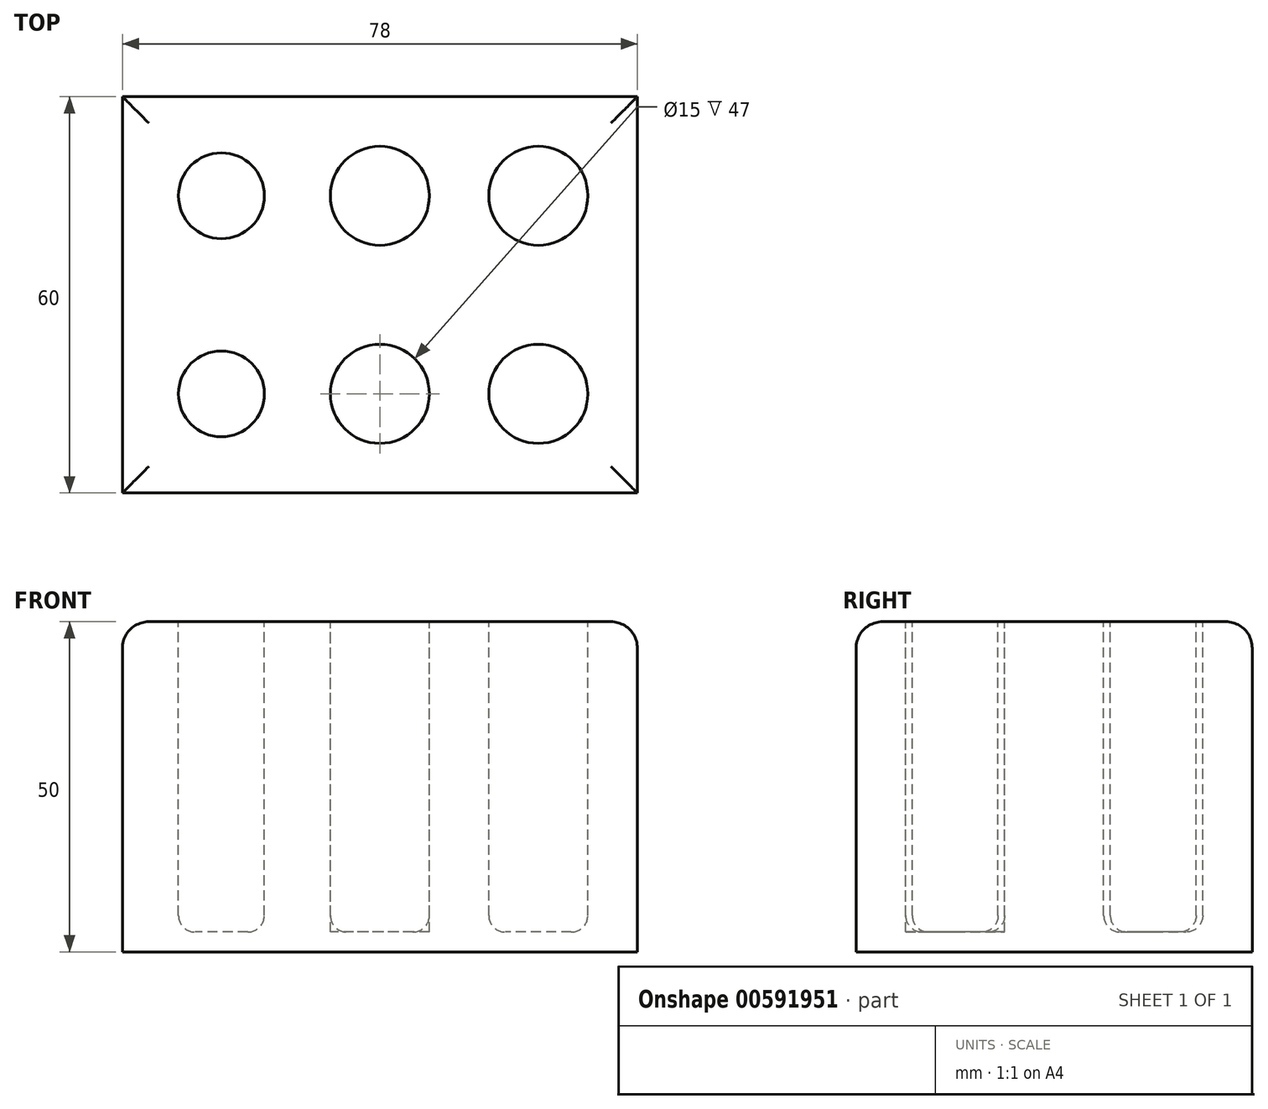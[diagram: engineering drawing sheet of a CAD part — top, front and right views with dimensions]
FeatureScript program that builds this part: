
annotation { "Feature Type Name" : "Feature", "Feature Type Description" : "" }
export const myFeature = defineFeature(function(context is Context, id is Id, definition is map)
    precondition{}
    {
        {
            var Q0;
            Q0=qCreatedBy(makeId("Top.planeOp"),FACE);
            var sketch = newSketch(context, id + "F0", { "sketchPlane" : qUnion([Q0])});
            skLineSegment(sketch, "E0.bottom", {"start": v(39, 30) * mm, "end": v(-39, 30) * mm});
            skLineSegment(sketch, "E0.top", {"start": v(39, -30) * mm, "end": v(-39, -30) * mm});
            skLineSegment(sketch, "E0.left", {"start": v(39, 30) * mm, "end": v(39, -30) * mm});
            skLineSegment(sketch, "E0.right", {"start": v(-39, 30) * mm, "end": v(-39, -30) * mm});
            skPoint(sketch, "E0.middle", {"position": v(0, 0) * mm});
            skCircle(sketch, "E1", {"center": v(-24, 15) * mm, "radius": 7.5 * mm});
            skCircle(sketch, "E2.0.1.0", {"center": v(-24, -15) * mm, "radius": 7.5 * mm});
            skCircle(sketch, "E2.1.0.0", {"center": v(0, 15) * mm, "radius": 7.5 * mm});
            skCircle(sketch, "E2.1.1.0", {"center": v(0, -15) * mm, "radius": 7.5 * mm});
            skCircle(sketch, "E2.2.0.0", {"center": v(24, 15) * mm, "radius": 7.5 * mm});
            skCircle(sketch, "E2.2.1.0", {"center": v(24, -15) * mm, "radius": 7.5 * mm});
            skLineSegment(sketch, "E2.direction1", {"start": v(-24, 15) * mm, "end": v(0, 15) * mm, "construction": true});
            skLineSegment(sketch, "E2.direction2", {"start": v(-24, 15) * mm, "end": v(-24, -15) * mm, "construction": true});
            skCircle(sketch, "E3", {"center": v(-24, 15) * mm, "radius": 6.5 * mm});
            skCircle(sketch, "E4", {"center": v(-24, -15) * mm, "radius": 6.5 * mm});
            skLineSegment(sketch, "E5", {"start": v(24, 30) * mm, "end": v(24, 15) * mm, "construction": true});
            skLineSegment(sketch, "E6", {"start": v(24, -15) * mm, "end": v(24, -30) * mm, "construction": true});
            skLineSegment(sketch, "E7", {"start": v(-24, -15) * mm, "end": v(-39, -15) * mm, "construction": true});
            skLineSegment(sketch, "E8", {"start": v(24, -15) * mm, "end": v(39, -15) * mm, "construction": true});
            skSolve(sketch);
        }
        {
            var Q0;
            Q0=makeQuery(id+"F0.imprint","IMPRINT",FACE,{"disambiguationData":[TD([[makeQuery(id+"F0.imprint","IMPRINT",EDGE,{"derivedFrom":sQuery(id+"F0.wireOp",EDGE,"E0.bottom")}),1.0]])]});
            var Q1;
            Q1=makeQuery(id+"F0.imprint","IMPRINT",FACE,{"disambiguationData":[TD([[makeQuery(id+"F0.imprint","IMPRINT",EDGE,{"derivedFrom":sQuery(id+"F0.wireOp",EDGE,"E2.6.1.0")}),1.0]])]});
            var Q2;
            Q2=makeQuery(id+"F0.imprint","IMPRINT",FACE,{"disambiguationData":[TD([[makeQuery(id+"F0.imprint","IMPRINT",EDGE,{"derivedFrom":sQuery(id+"F0.wireOp",EDGE,"E2.7.0.0")}),1.0]])]});
            var Q3;
            Q3=makeQuery(id+"F0.imprint","IMPRINT",FACE,{"disambiguationData":[TD([[makeQuery(id+"F0.imprint","IMPRINT",EDGE,{"derivedFrom":sQuery(id+"F0.wireOp",EDGE,"CZ0rmG6l-6SeH-jZlK-78gO-9g9mWHLpJfwp")}),1.0]])]});
            var Q4;
            Q4=makeQuery(id+"F0.imprint","IMPRINT",FACE,{"disambiguationData":[TD([[makeQuery(id+"F0.imprint","IMPRINT",EDGE,{"derivedFrom":sQuery(id+"F0.wireOp",EDGE,"EQraPTys-XXYO-9eC4-Nsuu-lk47bDu3l6d0")}),1.0]])]});
            var Q5;
            Q5=makeQuery(id+"F0.imprint","IMPRINT",FACE,{"disambiguationData":[TD([[makeQuery(id+"F0.imprint","IMPRINT",EDGE,{"derivedFrom":sQuery(id+"F0.wireOp",EDGE,"7bY6GpwJ-VG4l-dhhJ-CRH0-47noxeexM8H8")}),1.0]])]});
            var Q6;
            Q6=makeQuery(id+"F0.imprint","IMPRINT",FACE,{"disambiguationData":[TD([[makeQuery(id+"F0.imprint","IMPRINT",EDGE,{"derivedFrom":sQuery(id+"F0.wireOp",EDGE,"E1")}),1.0]])]});
            var Q7;
            Q7=makeQuery(id+"F0.imprint","IMPRINT",FACE,{"disambiguationData":[TD([[makeQuery(id+"F0.imprint","IMPRINT",EDGE,{"derivedFrom":sQuery(id+"F0.wireOp",EDGE,"E2.1.0.0")}),1.0]])]});
            var Q8;
            Q8=makeQuery(id+"F0.imprint","IMPRINT",FACE,{"disambiguationData":[TD([[makeQuery(id+"F0.imprint","IMPRINT",EDGE,{"derivedFrom":sQuery(id+"F0.wireOp",EDGE,"E2.2.0.0")}),1.0]])]});
            var Q9;
            Q9=makeQuery(id+"F0.imprint","IMPRINT",FACE,{"disambiguationData":[TD([[makeQuery(id+"F0.imprint","IMPRINT",EDGE,{"derivedFrom":sQuery(id+"F0.wireOp",EDGE,"E2.2.1.0")}),1.0]])]});
            var Q10;
            Q10=makeQuery(id+"F0.imprint","IMPRINT",FACE,{"disambiguationData":[TD([[makeQuery(id+"F0.imprint","IMPRINT",EDGE,{"derivedFrom":sQuery(id+"F0.wireOp",EDGE,"E2.3.0.0")}),1.0]])]});
            var Q11;
            Q11=makeQuery(id+"F0.imprint","IMPRINT",FACE,{"disambiguationData":[TD([[makeQuery(id+"F0.imprint","IMPRINT",EDGE,{"derivedFrom":sQuery(id+"F0.wireOp",EDGE,"E2.3.1.0")}),1.0]])]});
            var Q12;
            Q12=makeQuery(id+"F0.imprint","IMPRINT",FACE,{"disambiguationData":[TD([[makeQuery(id+"F0.imprint","IMPRINT",EDGE,{"derivedFrom":sQuery(id+"F0.wireOp",EDGE,"E2.4.0.0")}),1.0]])]});
            var Q13;
            Q13=makeQuery(id+"F0.imprint","IMPRINT",FACE,{"disambiguationData":[TD([[makeQuery(id+"F0.imprint","IMPRINT",EDGE,{"derivedFrom":sQuery(id+"F0.wireOp",EDGE,"E2.4.1.0")}),1.0]])]});
            var Q14;
            Q14=makeQuery(id+"F0.imprint","IMPRINT",FACE,{"disambiguationData":[TD([[makeQuery(id+"F0.imprint","IMPRINT",EDGE,{"derivedFrom":sQuery(id+"F0.wireOp",EDGE,"E2.5.0.0")}),1.0]])]});
            var Q15;
            Q15=makeQuery(id+"F0.imprint","IMPRINT",FACE,{"disambiguationData":[TD([[makeQuery(id+"F0.imprint","IMPRINT",EDGE,{"derivedFrom":sQuery(id+"F0.wireOp",EDGE,"E2.5.1.0")}),1.0]])]});
            var Q16;
            Q16=makeQuery(id+"F0.imprint","IMPRINT",FACE,{"disambiguationData":[TD([[makeQuery(id+"F0.imprint","IMPRINT",EDGE,{"derivedFrom":sQuery(id+"F0.wireOp",EDGE,"E2.6.0.0")}),1.0]])]});
            var Q17;
            Q17=makeQuery(id+"F0.imprint","IMPRINT",FACE,{"disambiguationData":[TD([[makeQuery(id+"F0.imprint","IMPRINT",EDGE,{"derivedFrom":sQuery(id+"F0.wireOp",EDGE,"E3")}),1.0]])]});
            var Q18;
            Q18=makeQuery(id+"F0.imprint","IMPRINT",FACE,{"disambiguationData":[TD([[makeQuery(id+"F0.imprint","IMPRINT",EDGE,{"derivedFrom":sQuery(id+"F0.wireOp",EDGE,"E4")}),1.0]])]});
            var Q19;
            Q19=makeQuery(id+"F0.imprint","IMPRINT",FACE,{"disambiguationData":[TD([[makeQuery(id+"F0.imprint","IMPRINT",EDGE,{"derivedFrom":sQuery(id+"F0.wireOp",EDGE,"2GA6yBS3-7ah5-xEHX-8kiC-7NQWTkTeTUZx")}),1.0]])]});
            var Q20;
            Q20=makeQuery(id+"F0.imprint","IMPRINT",FACE,{"disambiguationData":[TD([[makeQuery(id+"F0.imprint","IMPRINT",EDGE,{"derivedFrom":sQuery(id+"F0.wireOp",EDGE,"E2.7.1.0")}),1.0]])]});
            var Q21;
            Q21=makeQuery(id+"F0.imprint","IMPRINT",FACE,{"disambiguationData":[TD([[makeQuery(id+"F0.imprint","IMPRINT",EDGE,{"derivedFrom":sQuery(id+"F0.wireOp",EDGE,"E2.0.1.0")}),1.0]])]});
            var Q22;
            Q22=makeQuery(id+"F0.imprint","IMPRINT",FACE,{"disambiguationData":[TD([[makeQuery(id+"F0.imprint","IMPRINT",EDGE,{"derivedFrom":sQuery(id+"F0.wireOp",EDGE,"E2.1.1.0")}),1.0]])]});
            extrude(context, id + "F1", {"entities" : qUnion([Q0, Q1, Q2, Q3, Q4, Q5, Q6, Q7, Q8, Q9, Q10, Q11, Q12, Q13, Q14, Q15, Q16, Q17, Q18, Q19, Q20, Q21, Q22]), "oppositeDirection" : true, "depth" : 50 * mm, "offsetDistance" : 25 * mm});
        }
        {
            var Q0;
            Q0=makeQuery(id+"F0.imprint","IMPRINT",FACE,{"disambiguationData":[TD([[makeQuery(id+"F0.imprint","IMPRINT",EDGE,{"derivedFrom":sQuery(id+"F0.wireOp",EDGE,"E4")}),1.0]])]});
            var Q1;
            Q1=makeQuery(id+"F0.imprint","IMPRINT",FACE,{"disambiguationData":[TD([[makeQuery(id+"F0.imprint","IMPRINT",EDGE,{"derivedFrom":sQuery(id+"F0.wireOp",EDGE,"E3")}),1.0]])]});
            var Q2;
            Q2=makeQuery(id+"F0.imprint","IMPRINT",FACE,{"disambiguationData":[TD([[makeQuery(id+"F0.imprint","IMPRINT",EDGE,{"derivedFrom":sQuery(id+"F0.wireOp",EDGE,"E2.1.0.0")}),1.0]])]});
            var Q3;
            Q3=makeQuery(id+"F0.imprint","IMPRINT",FACE,{"disambiguationData":[TD([[makeQuery(id+"F0.imprint","IMPRINT",EDGE,{"derivedFrom":sQuery(id+"F0.wireOp",EDGE,"2GA6yBS3-7ah5-xEHX-8kiC-7NQWTkTeTUZx")}),1.0]])]});
            var Q4;
            Q4=makeQuery(id+"F0.imprint","IMPRINT",FACE,{"disambiguationData":[TD([[makeQuery(id+"F0.imprint","IMPRINT",EDGE,{"derivedFrom":sQuery(id+"F0.wireOp",EDGE,"E2.2.1.0")}),1.0]])]});
            var Q5;
            Q5=makeQuery(id+"F0.imprint","IMPRINT",FACE,{"disambiguationData":[TD([[makeQuery(id+"F0.imprint","IMPRINT",EDGE,{"derivedFrom":sQuery(id+"F0.wireOp",EDGE,"E2.2.0.0")}),1.0]])]});
            var Q6;
            Q6=makeQuery(id+"F0.imprint","IMPRINT",FACE,{"disambiguationData":[TD([[makeQuery(id+"F0.imprint","IMPRINT",EDGE,{"derivedFrom":sQuery(id+"F0.wireOp",EDGE,"E2.3.0.0")}),1.0]])]});
            var Q7;
            Q7=makeQuery(id+"F0.imprint","IMPRINT",FACE,{"disambiguationData":[TD([[makeQuery(id+"F0.imprint","IMPRINT",EDGE,{"derivedFrom":sQuery(id+"F0.wireOp",EDGE,"E2.3.1.0")}),1.0]])]});
            var Q8;
            Q8=makeQuery(id+"F0.imprint","IMPRINT",FACE,{"disambiguationData":[TD([[makeQuery(id+"F0.imprint","IMPRINT",EDGE,{"derivedFrom":sQuery(id+"F0.wireOp",EDGE,"E2.4.1.0")}),1.0]])]});
            var Q9;
            Q9=makeQuery(id+"F0.imprint","IMPRINT",FACE,{"disambiguationData":[TD([[makeQuery(id+"F0.imprint","IMPRINT",EDGE,{"derivedFrom":sQuery(id+"F0.wireOp",EDGE,"E2.4.0.0")}),1.0]])]});
            var Q10;
            Q10=makeQuery(id+"F0.imprint","IMPRINT",FACE,{"disambiguationData":[TD([[makeQuery(id+"F0.imprint","IMPRINT",EDGE,{"derivedFrom":sQuery(id+"F0.wireOp",EDGE,"E2.5.0.0")}),1.0]])]});
            var Q11;
            Q11=makeQuery(id+"F0.imprint","IMPRINT",FACE,{"disambiguationData":[TD([[makeQuery(id+"F0.imprint","IMPRINT",EDGE,{"derivedFrom":sQuery(id+"F0.wireOp",EDGE,"E2.6.0.0")}),1.0]])]});
            var Q12;
            Q12=makeQuery(id+"F0.imprint","IMPRINT",FACE,{"disambiguationData":[TD([[makeQuery(id+"F0.imprint","IMPRINT",EDGE,{"derivedFrom":sQuery(id+"F0.wireOp",EDGE,"CZ0rmG6l-6SeH-jZlK-78gO-9g9mWHLpJfwp")}),1.0]])]});
            var Q13;
            Q13=makeQuery(id+"F0.imprint","IMPRINT",FACE,{"disambiguationData":[TD([[makeQuery(id+"F0.imprint","IMPRINT",EDGE,{"derivedFrom":sQuery(id+"F0.wireOp",EDGE,"7bY6GpwJ-VG4l-dhhJ-CRH0-47noxeexM8H8")}),1.0]])]});
            var Q14;
            Q14=makeQuery(id+"F0.imprint","IMPRINT",FACE,{"disambiguationData":[TD([[makeQuery(id+"F0.imprint","IMPRINT",EDGE,{"derivedFrom":sQuery(id+"F0.wireOp",EDGE,"EQraPTys-XXYO-9eC4-Nsuu-lk47bDu3l6d0")}),1.0]])]});
            var Q15;
            Q15=makeQuery(id+"F0.imprint","IMPRINT",FACE,{"disambiguationData":[TD([[makeQuery(id+"F0.imprint","IMPRINT",EDGE,{"derivedFrom":sQuery(id+"F0.wireOp",EDGE,"E2.5.1.0")}),1.0]])]});
            var Q16;
            Q16=makeQuery(id+"F0.imprint","IMPRINT",FACE,{"disambiguationData":[TD([[makeQuery(id+"F0.imprint","IMPRINT",EDGE,{"derivedFrom":sQuery(id+"F0.wireOp",EDGE,"E2.1.1.0")}),1.0]])]});
            extrude(context, id + "F2", {"entities" : qUnion([Q0, Q1, Q2, Q3, Q4, Q5, Q6, Q7, Q8, Q9, Q10, Q11, Q12, Q13, Q14, Q15, Q16]), "operationType" : NewBodyOperationType.REMOVE, "oppositeDirection" : true, "depth" : 47 * mm, "offsetDistance" : 25 * mm});
        }
        {
            var Q0;
            Q0=makeQuery(id+"F1.opExtrude","CAP_EDGE",EDGE,{"disambiguationData":[OSD([sQuery(id+"F0.wireOp",EDGE,"E0.top")])],"isStart":true});
            var Q1;
            Q1=makeQuery(id+"F1.opExtrude","CAP_EDGE",EDGE,{"disambiguationData":[OSD([sQuery(id+"F0.wireOp",EDGE,"E0.left")])],"isStart":true});
            var Q2;
            Q2=makeQuery(id+"F1.opExtrude","CAP_EDGE",EDGE,{"disambiguationData":[OSD([sQuery(id+"F0.wireOp",EDGE,"E0.bottom")])],"isStart":true});
            var Q3;
            Q3=makeQuery(id+"F1.opExtrude","CAP_EDGE",EDGE,{"disambiguationData":[OSD([sQuery(id+"F0.wireOp",EDGE,"E0.right")])],"isStart":true});
            fillet(context, id + "F3", {"entities" : qUnion([Q0, Q1, Q2, Q3]), "radius" : 4 * mm, "tangentPropagation" : true, "allowEdgeOverflow" : false});
        }
        {
            var Q0;
            Q0=makeQuery(id+"F2.boolean.opBoolean","COPY",EDGE,{"derivedFrom":makeQuery(id+"F2.opExtrude","CAP_EDGE",EDGE,{"disambiguationData":[OSD([sQuery(id+"F0.wireOp",EDGE,"E2.5.0.0")])],"isStart":true})});
            var Q1;
            Q1=makeQuery(id+"F2.boolean.opBoolean","COPY",EDGE,{"derivedFrom":makeQuery(id+"F2.opExtrude","CAP_EDGE",EDGE,{"disambiguationData":[OSD([sQuery(id+"F0.wireOp",EDGE,"E2.2.1.0")])],"isStart":true})});
            var Q2;
            Q2=makeQuery(id+"F2.boolean.opBoolean","COPY",EDGE,{"derivedFrom":makeQuery(id+"F2.opExtrude","CAP_EDGE",EDGE,{"disambiguationData":[OSD([sQuery(id+"F0.wireOp",EDGE,"E2.1.0.0")])],"isStart":true})});
            var Q3;
            Q3=makeQuery(id+"F2.boolean.opBoolean","COPY",EDGE,{"derivedFrom":makeQuery(id+"F2.opExtrude","CAP_EDGE",EDGE,{"disambiguationData":[OSD([sQuery(id+"F0.wireOp",EDGE,"E2.4.0.0")])],"isStart":true})});
            var Q4;
            Q4=makeQuery(id+"F2.boolean.opBoolean","COPY",EDGE,{"derivedFrom":makeQuery(id+"F2.opExtrude","CAP_EDGE",EDGE,{"disambiguationData":[OSD([sQuery(id+"F0.wireOp",EDGE,"E2.2.0.0")])],"isStart":true})});
            var Q5;
            Q5=makeQuery(id+"F2.boolean.opBoolean","COPY",EDGE,{"derivedFrom":makeQuery(id+"F2.opExtrude","CAP_EDGE",EDGE,{"disambiguationData":[OSD([sQuery(id+"F0.wireOp",EDGE,"E2.6.0.0")])],"isStart":true})});
            var Q6;
            Q6=makeQuery(id+"F2.boolean.opBoolean","COPY",EDGE,{"derivedFrom":makeQuery(id+"F2.opExtrude","CAP_EDGE",EDGE,{"disambiguationData":[OSD([sQuery(id+"F0.wireOp",EDGE,"E2.3.1.0")])],"isStart":true})});
            var Q7;
            Q7=makeQuery(id+"F2.boolean.opBoolean","COPY",EDGE,{"derivedFrom":makeQuery(id+"F2.opExtrude","CAP_EDGE",EDGE,{"disambiguationData":[OSD([sQuery(id+"F0.wireOp",EDGE,"E2.5.1.0")])],"isStart":true})});
            var Q8;
            Q8=makeQuery(id+"F2.boolean.opBoolean","COPY",EDGE,{"derivedFrom":makeQuery(id+"F2.opExtrude","CAP_EDGE",EDGE,{"disambiguationData":[OSD([sQuery(id+"F0.wireOp",EDGE,"CZ0rmG6l-6SeH-jZlK-78gO-9g9mWHLpJfwp")])],"isStart":true})});
            var Q9;
            Q9=makeQuery(id+"F2.boolean.opBoolean","COPY",EDGE,{"derivedFrom":makeQuery(id+"F2.opExtrude","CAP_EDGE",EDGE,{"disambiguationData":[OSD([sQuery(id+"F0.wireOp",EDGE,"E2.4.1.0")])],"isStart":true})});
            var Q10;
            Q10=makeQuery(id+"F2.boolean.opBoolean","COPY",EDGE,{"derivedFrom":makeQuery(id+"F2.opExtrude","CAP_EDGE",EDGE,{"disambiguationData":[OSD([sQuery(id+"F0.wireOp",EDGE,"E2.3.0.0")])],"isStart":true})});
            var Q11;
            Q11=makeQuery(id+"F2.boolean.opBoolean","COPY",EDGE,{"derivedFrom":makeQuery(id+"F2.opExtrude","CAP_EDGE",EDGE,{"disambiguationData":[OSD([sQuery(id+"F0.wireOp",EDGE,"E3")])],"isStart":true})});
            var Q12;
            Q12=makeQuery(id+"F2.boolean.opBoolean","COPY",EDGE,{"derivedFrom":makeQuery(id+"F2.opExtrude","CAP_EDGE",EDGE,{"disambiguationData":[OSD([sQuery(id+"F0.wireOp",EDGE,"E4")])],"isStart":true})});
            var Q13;
            Q13=makeQuery(id+"F2.boolean.opBoolean","COPY",EDGE,{"derivedFrom":makeQuery(id+"F2.opExtrude","CAP_EDGE",EDGE,{"disambiguationData":[OSD([sQuery(id+"F0.wireOp",EDGE,"2GA6yBS3-7ah5-xEHX-8kiC-7NQWTkTeTUZx")])],"isStart":true})});
            var Q14;
            Q14=makeQuery(id+"F2.boolean.opBoolean","COPY",EDGE,{"derivedFrom":makeQuery(id+"F2.opExtrude","CAP_EDGE",EDGE,{"disambiguationData":[OSD([sQuery(id+"F0.wireOp",EDGE,"EQraPTys-XXYO-9eC4-Nsuu-lk47bDu3l6d0")])],"isStart":true})});
            var Q15;
            Q15=makeQuery(id+"F2.boolean.opBoolean","COPY",EDGE,{"derivedFrom":makeQuery(id+"F2.opExtrude","CAP_EDGE",EDGE,{"disambiguationData":[OSD([sQuery(id+"F0.wireOp",EDGE,"7bY6GpwJ-VG4l-dhhJ-CRH0-47noxeexM8H8")])],"isStart":true})});
            var Q16;
            Q16=makeQuery(id+"F2.boolean.opBoolean","COPY",EDGE,{"derivedFrom":makeQuery(id+"F2.opExtrude","CAP_EDGE",EDGE,{"disambiguationData":[OSD([sQuery(id+"F0.wireOp",EDGE,"E2.2.1.0")])],"isStart":false})});
            var Q17;
            Q17=makeQuery(id+"F2.boolean.opBoolean","COPY",EDGE,{"derivedFrom":makeQuery(id+"F2.opExtrude","CAP_EDGE",EDGE,{"disambiguationData":[OSD([sQuery(id+"F0.wireOp",EDGE,"E2.6.0.0")])],"isStart":false})});
            var Q18;
            Q18=makeQuery(id+"F2.boolean.opBoolean","COPY",EDGE,{"derivedFrom":makeQuery(id+"F2.opExtrude","CAP_EDGE",EDGE,{"disambiguationData":[OSD([sQuery(id+"F0.wireOp",EDGE,"7bY6GpwJ-VG4l-dhhJ-CRH0-47noxeexM8H8")])],"isStart":false})});
            var Q19;
            Q19=makeQuery(id+"F2.boolean.opBoolean","COPY",EDGE,{"derivedFrom":makeQuery(id+"F2.opExtrude","CAP_EDGE",EDGE,{"disambiguationData":[OSD([sQuery(id+"F0.wireOp",EDGE,"E2.3.0.0")])],"isStart":false})});
            var Q20;
            Q20=makeQuery(id+"F2.boolean.opBoolean","COPY",EDGE,{"derivedFrom":makeQuery(id+"F2.opExtrude","CAP_EDGE",EDGE,{"disambiguationData":[OSD([sQuery(id+"F0.wireOp",EDGE,"E2.4.0.0")])],"isStart":false})});
            var Q21;
            Q21=makeQuery(id+"F2.boolean.opBoolean","COPY",EDGE,{"derivedFrom":makeQuery(id+"F2.opExtrude","CAP_EDGE",EDGE,{"disambiguationData":[OSD([sQuery(id+"F0.wireOp",EDGE,"E2.5.1.0")])],"isStart":false})});
            var Q22;
            Q22=makeQuery(id+"F2.boolean.opBoolean","COPY",EDGE,{"derivedFrom":makeQuery(id+"F2.opExtrude","CAP_EDGE",EDGE,{"disambiguationData":[OSD([sQuery(id+"F0.wireOp",EDGE,"CZ0rmG6l-6SeH-jZlK-78gO-9g9mWHLpJfwp")])],"isStart":false})});
            var Q23;
            Q23=makeQuery(id+"F2.boolean.opBoolean","COPY",EDGE,{"derivedFrom":makeQuery(id+"F2.opExtrude","CAP_EDGE",EDGE,{"disambiguationData":[OSD([sQuery(id+"F0.wireOp",EDGE,"E2.3.1.0")])],"isStart":false})});
            var Q24;
            Q24=makeQuery(id+"F2.boolean.opBoolean","COPY",EDGE,{"derivedFrom":makeQuery(id+"F2.opExtrude","CAP_EDGE",EDGE,{"disambiguationData":[OSD([sQuery(id+"F0.wireOp",EDGE,"E2.2.0.0")])],"isStart":false})});
            var Q25;
            Q25=makeQuery(id+"F2.boolean.opBoolean","COPY",EDGE,{"derivedFrom":makeQuery(id+"F2.opExtrude","CAP_EDGE",EDGE,{"disambiguationData":[OSD([sQuery(id+"F0.wireOp",EDGE,"E3")])],"isStart":false})});
            var Q26;
            Q26=makeQuery(id+"F2.boolean.opBoolean","COPY",EDGE,{"derivedFrom":makeQuery(id+"F2.opExtrude","CAP_EDGE",EDGE,{"disambiguationData":[OSD([sQuery(id+"F0.wireOp",EDGE,"E2.1.0.0")])],"isStart":false})});
            var Q27;
            Q27=makeQuery(id+"F2.boolean.opBoolean","COPY",EDGE,{"derivedFrom":makeQuery(id+"F2.opExtrude","CAP_EDGE",EDGE,{"disambiguationData":[OSD([sQuery(id+"F0.wireOp",EDGE,"E2.5.0.0")])],"isStart":false})});
            var Q28;
            Q28=makeQuery(id+"F2.boolean.opBoolean","COPY",EDGE,{"derivedFrom":makeQuery(id+"F2.opExtrude","CAP_EDGE",EDGE,{"disambiguationData":[OSD([sQuery(id+"F0.wireOp",EDGE,"E2.4.1.0")])],"isStart":false})});
            var Q29;
            Q29=makeQuery(id+"F2.boolean.opBoolean","COPY",EDGE,{"derivedFrom":makeQuery(id+"F2.opExtrude","CAP_EDGE",EDGE,{"disambiguationData":[OSD([sQuery(id+"F0.wireOp",EDGE,"E4")])],"isStart":false})});
            var Q30;
            Q30=makeQuery(id+"F2.boolean.opBoolean","COPY",EDGE,{"derivedFrom":makeQuery(id+"F2.opExtrude","CAP_EDGE",EDGE,{"disambiguationData":[OSD([sQuery(id+"F0.wireOp",EDGE,"2GA6yBS3-7ah5-xEHX-8kiC-7NQWTkTeTUZx")])],"isStart":false})});
            var Q31;
            Q31=makeQuery(id+"F2.boolean.opBoolean","COPY",EDGE,{"derivedFrom":makeQuery(id+"F2.opExtrude","CAP_EDGE",EDGE,{"disambiguationData":[OSD([sQuery(id+"F0.wireOp",EDGE,"EQraPTys-XXYO-9eC4-Nsuu-lk47bDu3l6d0")])],"isStart":false})});
            var Q32;
            Q32=makeQuery(id+"F2.boolean.opBoolean","COPY",EDGE,{"derivedFrom":makeQuery(id+"F2.opExtrude","CAP_EDGE",EDGE,{"disambiguationData":[OSD([sQuery(id+"F0.wireOp",EDGE,"E2.1.1.0")])],"isStart":true})});
            fillet(context, id + "F4", {"entities" : qUnion([Q0, Q1, Q2, Q3, Q4, Q5, Q6, Q7, Q8, Q9, Q10, Q11, Q12, Q13, Q14, Q15, Q16, Q17, Q18, Q19, Q20, Q21, Q22, Q23, Q24, Q25, Q26, Q27, Q28, Q29, Q30, Q31, Q32]), "radius" : 2.5 * mm, "tangentPropagation" : true, "allowEdgeOverflow" : false});
        }
    });
